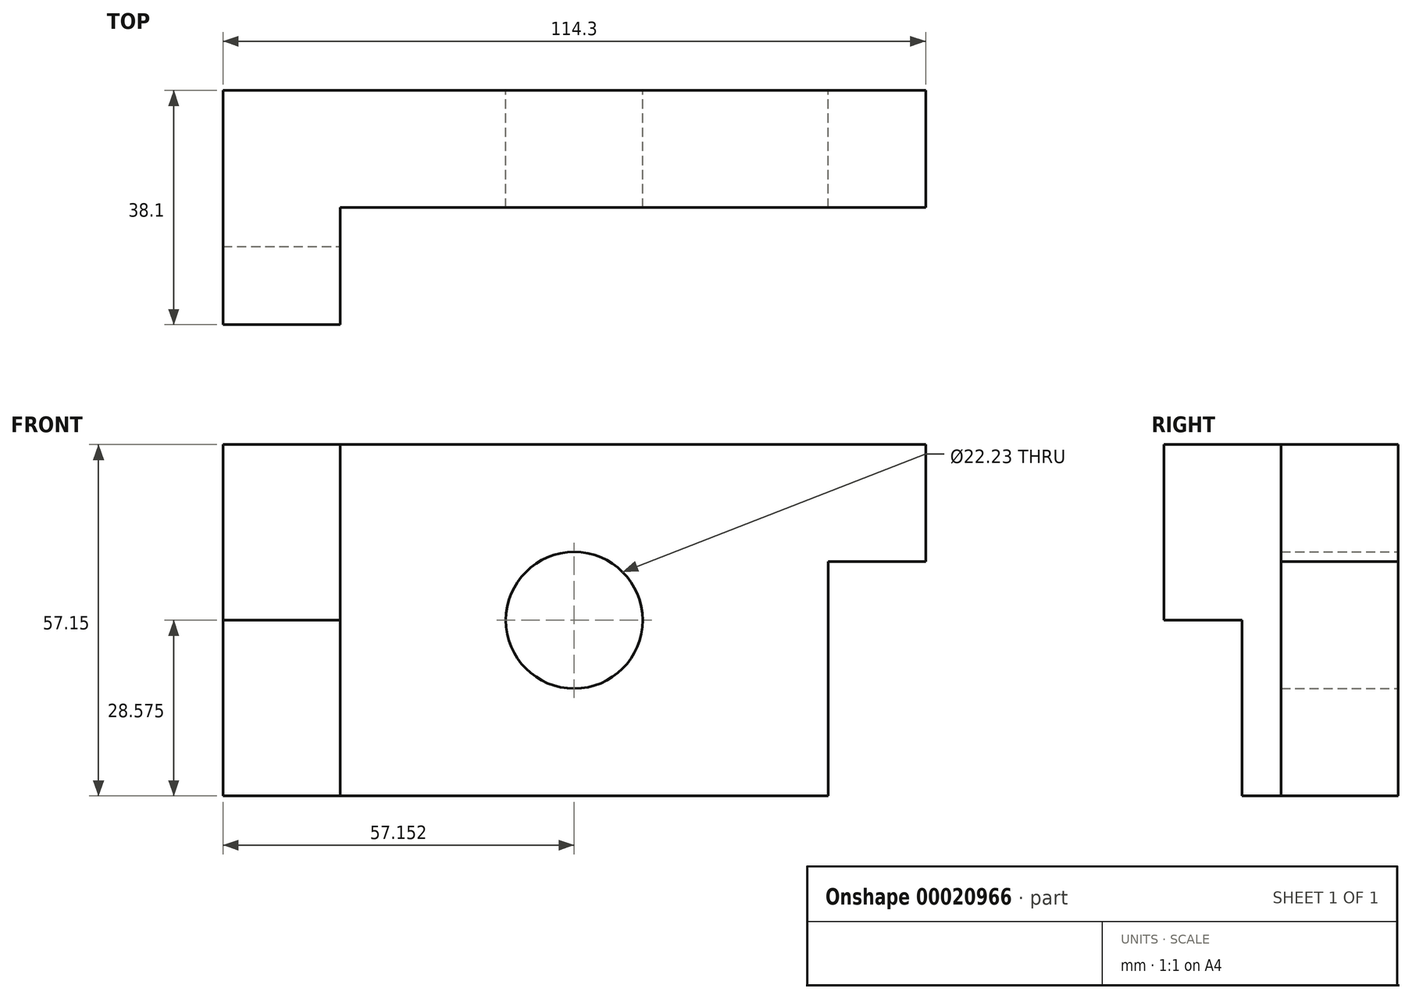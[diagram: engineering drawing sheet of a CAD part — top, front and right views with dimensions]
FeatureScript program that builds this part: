
annotation { "Feature Type Name" : "Feature", "Feature Type Description" : "" }
export const myFeature = defineFeature(function(context is Context, id is Id, definition is map)
    precondition{}
    {
        {
            var Q0;
            Q0=qCreatedBy(makeId("Front.planeOp"),FACE);
            var sketch = newSketch(context, id + "F0", { "sketchPlane" : qUnion([Q0])});
            skLineSegment(sketch, "E0.bottom", {"start": v(-57.45, 39.28) * mm, "end": v(-38.4, 39.28) * mm});
            skLineSegment(sketch, "E0.top", {"start": v(-57.45, -17.87) * mm, "end": v(40.98, -17.87) * mm});
            skLineSegment(sketch, "E0.left", {"start": v(-57.45, 39.28) * mm, "end": v(-57.45, 10.7) * mm});
            skLineSegment(sketch, "E0.right", {"start": v(56.85, 39.28) * mm, "end": v(56.85, 20.23) * mm});
            skLineSegment(sketch, "E1.top", {"start": v(56.85, 20.23) * mm, "end": v(40.98, 20.23) * mm});
            skLineSegment(sketch, "E1.right", {"start": v(40.98, -17.87) * mm, "end": v(40.98, 20.23) * mm});
            skLineSegment(sketch, "E2", {"start": v(-38.4, 39.28) * mm, "end": v(-38.4, -17.87) * mm});
            skLineSegment(sketch, "E3", {"start": v(-57.45, 10.7) * mm, "end": v(-38.4, 10.7) * mm});
            skLineSegment(sketch, "E4", {"start": v(-57.45, 10.7) * mm, "end": v(-57.45, -17.87) * mm});
            skLineSegment(sketch, "E5", {"start": v(-0.3, 39.28) * mm, "end": v(56.85, 39.28) * mm});
            skLineSegment(sketch, "E6", {"start": v(-0.3, 39.28) * mm, "end": v(-38.4, 39.28) * mm});
            skCircle(sketch, "E7", {"center": v(-0.3, 10.7) * mm, "radius": 11.11 * mm});
            skPoint(sketch, "E8.trimOffspring.end.orphan", {"position": v(-0.3, -17.87) * mm});
            skSolve(sketch);
        }
        {
            var Q0;
            {var subQ2=sQuery(id+"F0.wireOp",EDGE,"E0.bottom");Q0=makeQuery(id+"F0.imprint","IMPRINT",FACE,{"disambiguationData":[TD([[makeQuery(id+"F0.imprint","IMPRINT",EDGE,{"derivedFrom":subQ2}),-1.0]])]});}
            extrude(context, id + "F1", {"entities" : qUnion([Q0]), "depth" : 38.1 * mm});
        }
        {
            var Q0;
            {var subQ1=sQuery(id+"F0.wireOp",EDGE,"E3");Q0=makeQuery(id+"F0.imprint","IMPRINT",FACE,{"disambiguationData":[TD([[makeQuery(id+"F0.imprint","IMPRINT",EDGE,{"derivedFrom":subQ1}),-1.0]])]});}
            extrude(context, id + "F2", {"entities" : qUnion([Q0]), "operationType" : NewBodyOperationType.ADD, "depth" : 25.4 * mm});
        }
        {
            var Q0;
            Q0=makeQuery(id+"F0.imprint","IMPRINT",FACE,{"disambiguationData":[TD([[makeQuery(id+"F0.imprint","IMPRINT",EDGE,{"derivedFrom":sQuery(id+"F0.wireOp",EDGE,"E0.right")}),-1.0]])]});
            extrude(context, id + "F3", {"entities" : qUnion([Q0]), "operationType" : NewBodyOperationType.ADD, "depth" : 19.05 * mm});
        }
    });
